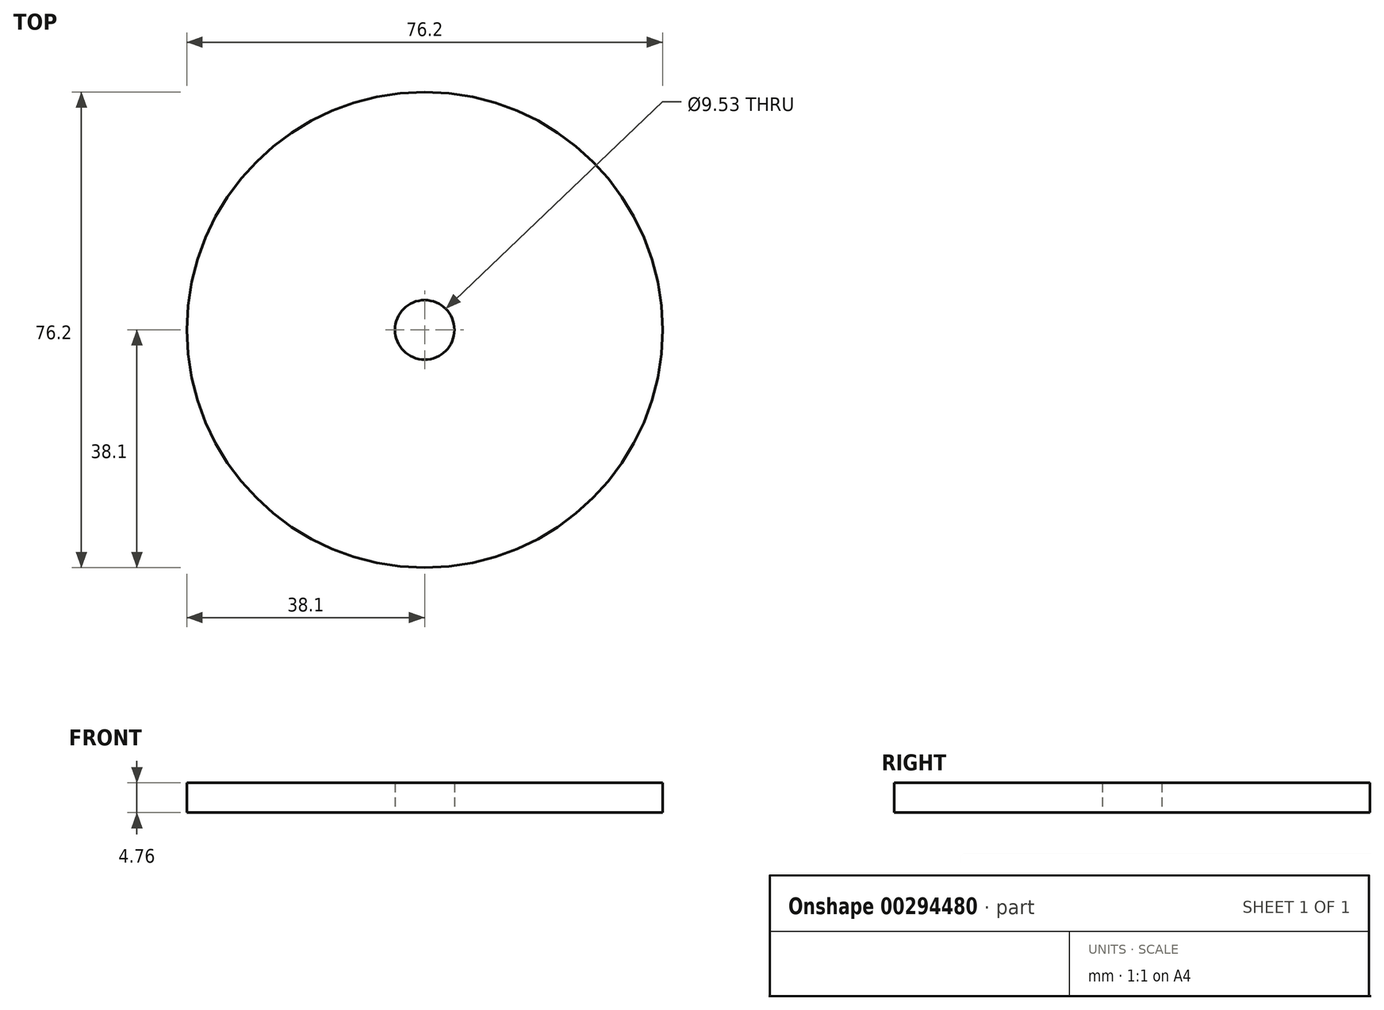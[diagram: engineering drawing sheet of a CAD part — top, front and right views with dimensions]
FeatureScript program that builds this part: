
annotation { "Feature Type Name" : "Feature", "Feature Type Description" : "" }
export const myFeature = defineFeature(function(context is Context, id is Id, definition is map)
    precondition{}
    {
        {
            var Q0;
            Q0=qCreatedBy(makeId("Top.planeOp"),FACE);
            var sketch = newSketch(context, id + "F0", { "sketchPlane" : qUnion([Q0])});
            skCircle(sketch, "E0", {"center": v(0, 0) * mm, "radius": 38.1 * mm});
            skCircle(sketch, "E1", {"center": v(0, 0) * mm, "radius": 4.76 * mm});
            skLineSegment(sketch, "E2", {"start": v(-18.77, 33.16) * mm, "end": v(-0.37, 38.1) * mm});
            skLineSegment(sketch, "E3", {"start": v(-0.37, 38.1) * mm, "end": v(0, 0) * mm});
            skLineSegment(sketch, "E4", {"start": v(-18.77, 33.16) * mm, "end": v(0, 0) * mm});
            skSolve(sketch);
        }
        {
            var Q0;
            Q0 = qSketchRegion(id + "F0", true);
            extrude(context, id + "F1", {"entities" : qUnion([Q0]), "depth" : 4.76 * mm});
        }
    });
